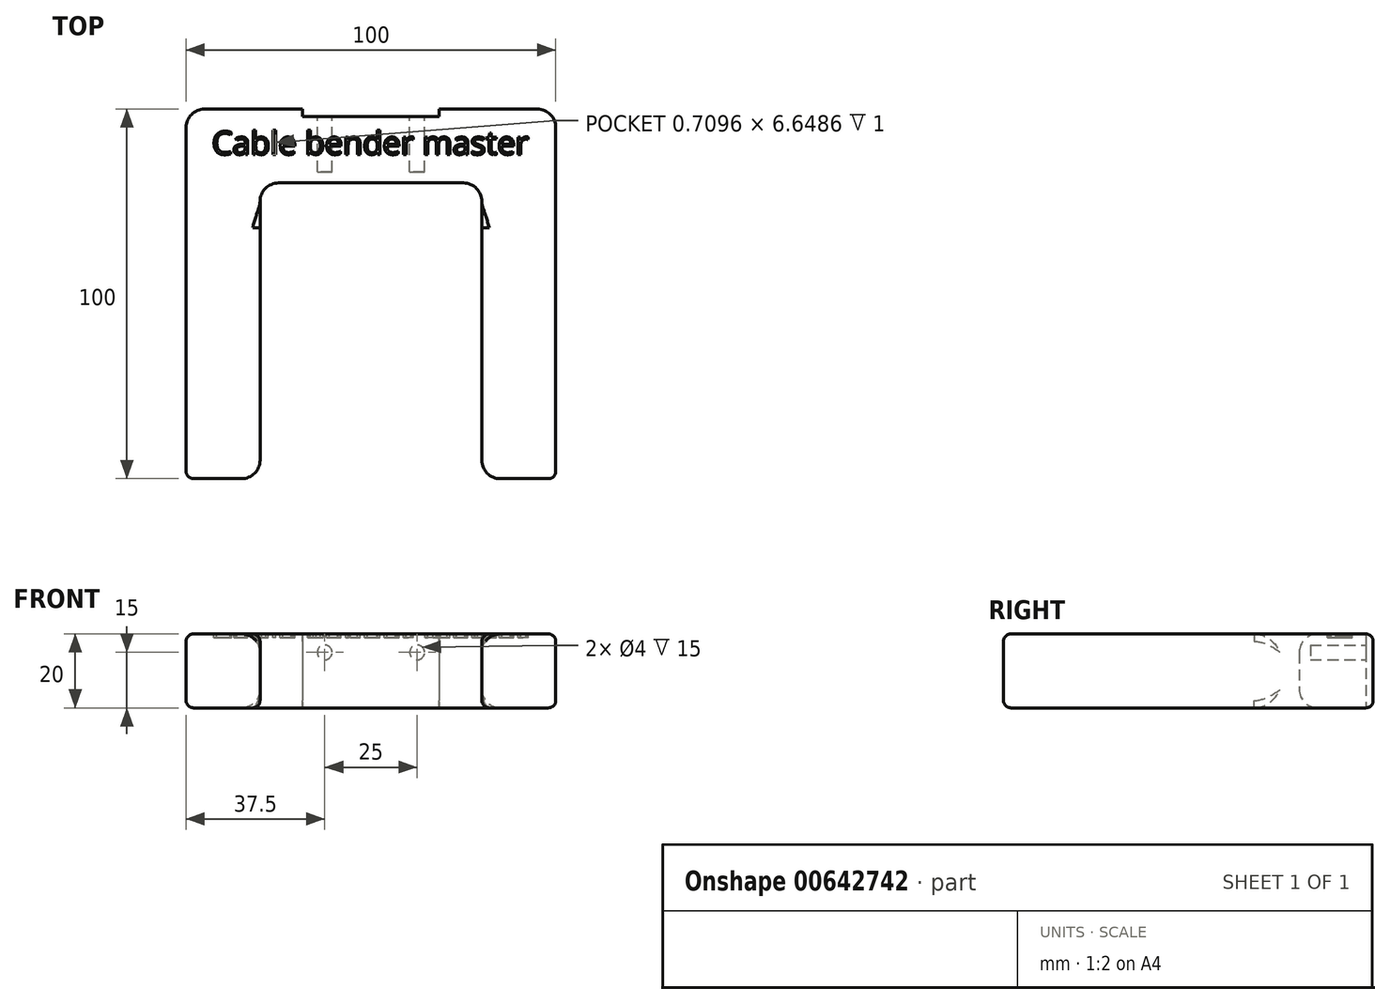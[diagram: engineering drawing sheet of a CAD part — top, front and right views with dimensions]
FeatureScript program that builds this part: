
annotation { "Feature Type Name" : "Feature", "Feature Type Description" : "" }
export const myFeature = defineFeature(function(context is Context, id is Id, definition is map)
    precondition{}
    {
        {
            var Q0;
            Q0=qCreatedBy(makeId("Top.planeOp"),FACE);
            var sketch = newSketch(context, id + "F0", { "sketchPlane" : qUnion([Q0])});
            skLineSegment(sketch, "E0.bottom", {"start": v(-50, 0) * mm, "end": v(-18.5, 0) * mm});
            skLineSegment(sketch, "E0.top", {"start": v(-50, -100) * mm, "end": v(-30, -100) * mm});
            skLineSegment(sketch, "E0.left", {"start": v(-50, 0) * mm, "end": v(-50, -100) * mm});
            skLineSegment(sketch, "E0.right", {"start": v(50, 0) * mm, "end": v(50, -100) * mm});
            skLineSegment(sketch, "E1.top", {"start": v(-30, -20) * mm, "end": v(30, -20) * mm});
            skLineSegment(sketch, "E1.left", {"start": v(-30, -100) * mm, "end": v(-30, -20) * mm});
            skLineSegment(sketch, "E1.right", {"start": v(30, -100) * mm, "end": v(30, -20) * mm});
            skLineSegment(sketch, "E2.trimOffspring", {"start": v(30, -100) * mm, "end": v(50, -100) * mm});
            skLineSegment(sketch, "E3.top", {"start": v(-18.5, -2) * mm, "end": v(18.5, -2) * mm});
            skLineSegment(sketch, "E3.left", {"start": v(-18.5, 0) * mm, "end": v(-18.5, -2) * mm});
            skLineSegment(sketch, "E3.right", {"start": v(18.5, 0) * mm, "end": v(18.5, -2) * mm});
            skLineSegment(sketch, "E4.trimOffspring", {"start": v(18.5, 0) * mm, "end": v(50, 0) * mm});
            skSolve(sketch);
        }
        {
            var Q0;
            Q0 = qSketchRegion(id + "F0", true);
            extrude(context, id + "F1", {"entities" : qUnion([Q0]), "depth" : 10 * mm, "offsetDistance" : 25 * mm, "hasSecondDirection" : true, "secondDirectionOppositeDirection" : true, "secondDirectionDepth" : 10 * mm});
        }
        {
            var Q0;
            Q0=makeQuery(id+"F1.opExtrude","SWEPT_FACE",FACE,{"disambiguationData":[OSD([sQuery(id+"F0.wireOp",EDGE,"E3.top")])]});
            var sketch = newSketch(context, id + "F2", { "sketchPlane" : qUnion([Q0])});
            skCircle(sketch, "E5", {"center": v(-12.5, 5) * mm, "radius": 2 * mm});
            skCircle(sketch, "E6", {"center": v(12.5, 5) * mm, "radius": 2 * mm});
            skSolve(sketch);
        }
        {
            var Q0;
            Q0 = qSketchRegion(id + "F2", true);
            extrude(context, id + "F3", {"entities" : qUnion([Q0]), "operationType" : NewBodyOperationType.REMOVE, "oppositeDirection" : true, "depth" : 15 * mm, "offsetDistance" : 25 * mm});
        }
        {
            var Q0;
            Q0=makeQuery(id+"F1.opExtrude","SWEPT_EDGE",EDGE,{"disambiguationData":[OSD([sQuery(id+"F0.wireOp",EDGE,"E0.right"),sQuery(id+"F0.wireOp",EDGE,"E4.trimOffspring")])]});
            var Q1;
            Q1=makeQuery(id+"F1.opExtrude","SWEPT_EDGE",EDGE,{"disambiguationData":[OSD([sQuery(id+"F0.wireOp",EDGE,"E0.bottom"),sQuery(id+"F0.wireOp",EDGE,"E0.left")])]});
            var Q2;
            Q2=makeQuery(id+"F1.opExtrude","SWEPT_EDGE",EDGE,{"disambiguationData":[OSD([sQuery(id+"F0.wireOp",EDGE,"E0.top"),sQuery(id+"F0.wireOp",EDGE,"E1.left")])]});
            var Q3;
            Q3=makeQuery(id+"F1.opExtrude","SWEPT_EDGE",EDGE,{"disambiguationData":[OSD([sQuery(id+"F0.wireOp",EDGE,"E1.right"),sQuery(id+"F0.wireOp",EDGE,"E2.trimOffspring")])]});
            var Q4;
            Q4=makeQuery(id+"F1.opExtrude","SWEPT_EDGE",EDGE,{"disambiguationData":[OSD([sQuery(id+"F0.wireOp",EDGE,"E1.top"),sQuery(id+"F0.wireOp",EDGE,"E1.right")])]});
            var Q5;
            Q5=makeQuery(id+"F1.opExtrude","SWEPT_EDGE",EDGE,{"disambiguationData":[OSD([sQuery(id+"F0.wireOp",EDGE,"E1.top"),sQuery(id+"F0.wireOp",EDGE,"E1.left")])]});
            var Q6;
            Q6=makeQuery(id+"F1.opExtrude","CAP_EDGE",EDGE,{"disambiguationData":[OSD([sQuery(id+"F0.wireOp",EDGE,"E1.top")])],"isStart":true});
            var Q7;
            Q7=makeQuery(id+"F1.opExtrude","CAP_EDGE",EDGE,{"disambiguationData":[OSD([sQuery(id+"F0.wireOp",EDGE,"E1.top")])],"isStart":false});
            fillet(context, id + "F4", {"entities" : qUnion([Q0, Q1, Q2, Q3, Q4, Q5, Q6, Q7]), "radius" : 5 * mm, "tangentPropagation" : true, "allowEdgeOverflow" : false});
        }
        {
            var Q0;
            Q0=makeQuery(id+"F1.opExtrude","SWEPT_FACE",FACE,{"disambiguationData":[OSD([sQuery(id+"F0.wireOp",EDGE,"E0.right")])]});
            var Q1;
            Q1=makeQuery(id+"F1.opExtrude","SWEPT_FACE",FACE,{"disambiguationData":[OSD([sQuery(id+"F0.wireOp",EDGE,"E2.trimOffspring")])]});
            var Q2;
            Q2=makeQuery(id+"F1.opExtrude","SWEPT_FACE",FACE,{"disambiguationData":[OSD([sQuery(id+"F0.wireOp",EDGE,"E0.left")])]});
            var Q3;
            Q3=makeQuery(id+"F1.opExtrude","SWEPT_FACE",FACE,{"disambiguationData":[OSD([sQuery(id+"F0.wireOp",EDGE,"E0.top")])]});
            fillet(context, id + "F5", {"entities" : qUnion([Q0, Q1, Q2, Q3]), "radius" : 2 * mm, "tangentPropagation" : true, "allowEdgeOverflow" : false});
        }
        {
            var Q0;
            Q0=makeQuery(id+"F1.opExtrude","CAP_FACE",FACE,{"disambiguationData":[OSD([sQuery(id+"F0.wireOp",EDGE,"E0.bottom"),sQuery(id+"F0.wireOp",EDGE,"E0.top"),sQuery(id+"F0.wireOp",EDGE,"E0.left"),sQuery(id+"F0.wireOp",EDGE,"E0.right"),sQuery(id+"F0.wireOp",EDGE,"E1.top"),sQuery(id+"F0.wireOp",EDGE,"E1.left"),sQuery(id+"F0.wireOp",EDGE,"E1.right"),sQuery(id+"F0.wireOp",EDGE,"E2.trimOffspring"),sQuery(id+"F0.wireOp",EDGE,"E3.top"),sQuery(id+"F0.wireOp",EDGE,"E3.left"),sQuery(id+"F0.wireOp",EDGE,"E3.right"),sQuery(id+"F0.wireOp",EDGE,"E4.trimOffspring")])],"isStart":false});
            var sketch = newSketch(context, id + "F6", { "sketchPlane" : qUnion([Q0])});
            skText(sketch, "E7", { "text": "Cable bender master", "fontName": "OpenSans-Regular.ttf"});
            const initialGuessF6  = {"E7": [-0.043, -0.0123, 1, 0, 0.0063]};
            skSetInitialGuess(sketch, initialGuessF6);
            skSolve(sketch);
        }
        {
            var Q0;
            Q0 = qSketchRegion(id + "F6", true);
            extrude(context, id + "F7", {"entities" : qUnion([Q0]), "operationType" : NewBodyOperationType.REMOVE, "oppositeDirection" : true, "depth" : 1 * mm, "offsetDistance" : 25 * mm});
        }
    });
